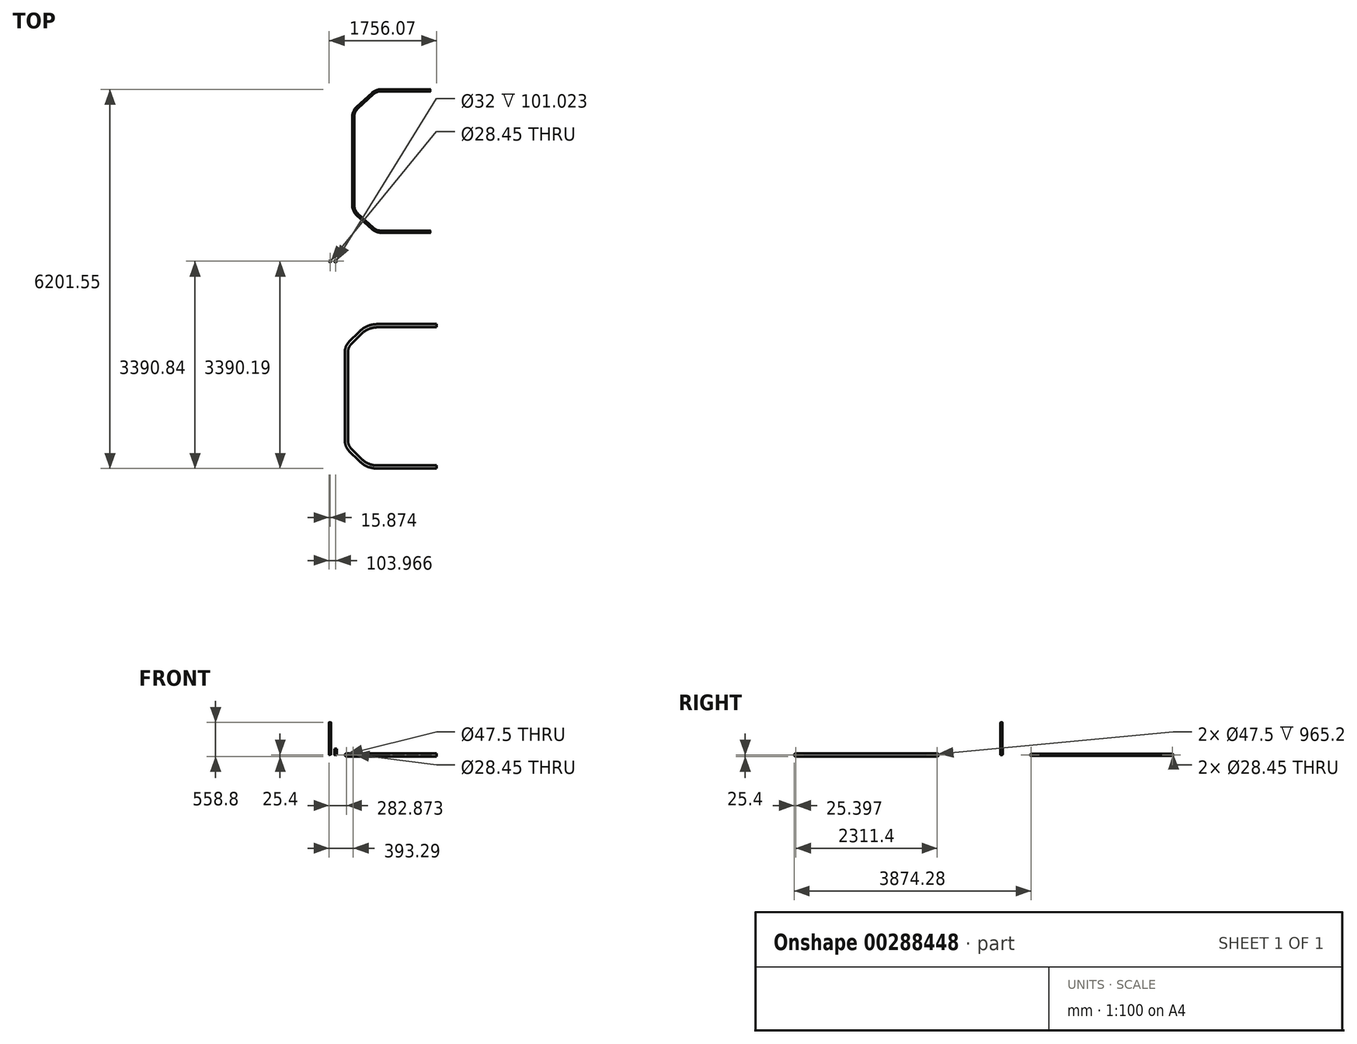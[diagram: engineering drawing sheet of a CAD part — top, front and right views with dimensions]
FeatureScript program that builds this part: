
annotation { "Feature Type Name" : "Feature", "Feature Type Description" : "" }
export const myFeature = defineFeature(function(context is Context, id is Id, definition is map)
    precondition{}
    {
        {
            var Q0;
            Q0=qCreatedBy(makeId("Top.planeOp"),FACE);
            var sketch = newSketch(context, id + "F0", { "sketchPlane" : qUnion([Q0])});
            skLineSegment(sketch, "E0", {"start": v(-110.42, -2096.28) * mm, "end": v(1362.78, -2096.28) * mm, "construction": true});
            skLineSegment(sketch, "E1", {"start": v(1362.78, -2096.28) * mm, "end": v(1362.78, -3251.98) * mm, "construction": true});
            skLineSegment(sketch, "E2", {"start": v(1362.78, -3251.98) * mm, "end": v(397.58, -3251.98) * mm});
            skLineSegment(sketch, "E3", {"start": v(115.74, -3135.24) * mm, "end": v(-50.9, -2968.6) * mm});
            skLineSegment(sketch, "E4", {"start": v(-110.42, -2824.91) * mm, "end": v(-110.42, -2096.28) * mm});
            skPoint(sketch, "E5.visualSharp", {"position": v(-110.42, -2909.08) * mm});
            skArc(sketch, "E5.filletArc", {"start": v(-110.42, -2824.91) * mm, "mid": v(-94.95, -2902.68) * mm, "end": v(-50.9, -2968.6) * mm});
            skPoint(sketch, "E6.visualSharp", {"position": v(232.48, -3251.98) * mm});
            skArc(sketch, "E6.filletArc", {"start": v(115.74, -3135.24) * mm, "mid": v(245.05, -3221.64) * mm, "end": v(397.58, -3251.98) * mm});
            skLineSegment(sketch, "E7.MirrorCS", {"start": v(-110.42, -1367.65) * mm, "end": v(-110.42, -2096.28) * mm});
            skArc(sketch, "E8.MirrorCS", {"start": v(-110.42, -1367.65) * mm, "mid": v(-94.95, -1289.9) * mm, "end": v(-50.9, -1223.97) * mm});
            skLineSegment(sketch, "E9.MirrorCS", {"start": v(115.74, -1057.33) * mm, "end": v(-50.9, -1223.97) * mm});
            skLineSegment(sketch, "E10.MirrorCS", {"start": v(1362.78, -940.58) * mm, "end": v(397.58, -940.58) * mm});
            skArc(sketch, "E11.MirrorCS", {"start": v(115.74, -1057.33) * mm, "mid": v(245.05, -970.92) * mm, "end": v(397.58, -940.58) * mm});
            skPoint(sketch, "E12.MirrorP", {"position": v(232.48, -940.58) * mm});
            skPoint(sketch, "E13.MirrorP", {"position": v(-110.42, -1283.48) * mm});
            skCircle(sketch, "E14", {"center": v(1203.51, -3251.98) * mm, "radius": 16 * mm});
            skCircle(sketch, "E15.0", {"center": v(1203.51, -3251.98) * mm, "radius": 17.65 * mm});
            skSolve(sketch);
        }
        {
            var Q0;
            Q0=qCreatedBy(makeId("Top.planeOp"),FACE);
            var sketch = newSketch(context, id + "F1", { "sketchPlane" : qUnion([Q0])});
            skLineSegment(sketch, "E16", {"start": v(0, 1752.6) * mm, "end": v(1270, 1752.6) * mm, "construction": true});
            skLineSegment(sketch, "E17", {"start": v(1270, 1752.6) * mm, "end": v(1270, 596.9) * mm, "construction": true});
            skLineSegment(sketch, "E18", {"start": v(1270, 596.9) * mm, "end": v(453.74, 596.9) * mm});
            skLineSegment(sketch, "E19", {"start": v(316.58, 650.18) * mm, "end": v(66.04, 879.38) * mm});
            skLineSegment(sketch, "E20", {"start": v(0, 1029.3) * mm, "end": v(0, 1752.6) * mm});
            skPoint(sketch, "E21.visualSharp", {"position": v(0, 939.8) * mm});
            skArc(sketch, "E21.filletArc", {"start": v(0, 1029.3) * mm, "mid": v(17.24, 947.4) * mm, "end": v(66.04, 879.38) * mm});
            skPoint(sketch, "E22.visualSharp", {"position": v(374.81, 596.9) * mm});
            skArc(sketch, "E22.filletArc", {"start": v(316.58, 650.18) * mm, "mid": v(380.17, 610.69) * mm, "end": v(453.74, 596.9) * mm});
            skLineSegment(sketch, "E23.MirrorCS", {"start": v(0, 2475.9) * mm, "end": v(0, 1752.6) * mm});
            skArc(sketch, "E24.MirrorCS", {"start": v(0, 2475.9) * mm, "mid": v(17.24, 2557.8) * mm, "end": v(66.04, 2625.82) * mm});
            skLineSegment(sketch, "E25.MirrorCS", {"start": v(316.58, 2855.02) * mm, "end": v(66.04, 2625.82) * mm});
            skLineSegment(sketch, "E26.MirrorCS", {"start": v(1270, 2908.3) * mm, "end": v(453.74, 2908.3) * mm});
            skArc(sketch, "E27.MirrorCS", {"start": v(316.58, 2855.02) * mm, "mid": v(380.17, 2894.51) * mm, "end": v(453.74, 2908.3) * mm});
            skPoint(sketch, "E28.MirrorP", {"position": v(374.81, 2908.3) * mm});
            skPoint(sketch, "E29.MirrorP", {"position": v(0, 2565.4) * mm});
            skSolve(sketch);
        }
        {
            var Q0;
            Q0=sQuery(id+"F0.wireOp",EDGE,"E1");
            cPlane(context, id + "F2", {"entities" : qUnion([Q0]), "cplaneType" : CPlaneType.LINE_ANGLE, "offset" : 25.4 * mm, "angle" : 90 * degree, "width" : 152.4 * mm, "height" : 152.4 * mm});
        }
        {
            var Q0;
            Q0=qCreatedBy(id+"F2.planeOp",FACE);
            var sketch = newSketch(context, id + "F3", { "sketchPlane" : qUnion([Q0])});
            skPoint(sketch, "E30.0", {"position": v(-3251.98, 0) * mm});
            skCircle(sketch, "E31", {"center": v(-3251.98, 0) * mm, "radius": 25.4 * mm});
            skCircle(sketch, "E32.0", {"center": v(-3251.98, 0) * mm, "radius": 23.75 * mm});
            skSolve(sketch);
        }
        {
            var Q0;
            Q0=makeQuery(id+"F3.imprint","IMPRINT",FACE,{"disambiguationData":[TD([[makeQuery(id+"F3.imprint","IMPRINT",EDGE,{"derivedFrom":sQuery(id+"F3.wireOp",EDGE,"E31")}),1.0]])]});
            var Q1;
            Q1=sQuery(id+"F0.wireOp",EDGE,"E2");
            var Q2;
            Q2=sQuery(id+"F0.wireOp",EDGE,"E6.filletArc");
            var Q3;
            Q3=sQuery(id+"F0.wireOp",EDGE,"E3");
            var Q4;
            Q4=sQuery(id+"F0.wireOp",EDGE,"E5.filletArc");
            var Q5;
            Q5=sQuery(id+"F0.wireOp",EDGE,"E4");
            var Q6;
            Q6=sQuery(id+"F0.wireOp",EDGE,"E7.MirrorCS");
            var Q7;
            Q7=sQuery(id+"F0.wireOp",EDGE,"E8.MirrorCS");
            var Q8;
            Q8=sQuery(id+"F0.wireOp",EDGE,"E9.MirrorCS");
            var Q9;
            Q9=sQuery(id+"F0.wireOp",EDGE,"E11.MirrorCS");
            var Q10;
            Q10=sQuery(id+"F0.wireOp",EDGE,"E10.MirrorCS");
            sweep(context, id + "F4", {"profiles" : qUnion([Q0]), "path" : qUnion([Q1, Q2, Q3, Q4, Q5, Q6, Q7, Q8, Q9, Q10])});
        }
        {
            var Q0;
            Q0=sQuery(id+"F1.wireOp",EDGE,"E17");
            cPlane(context, id + "F5", {"entities" : qUnion([Q0]), "cplaneType" : CPlaneType.LINE_ANGLE, "offset" : 25.4 * mm, "angle" : 90 * degree, "width" : 152.4 * mm, "height" : 152.4 * mm});
        }
        {
            var Q0;
            Q0=qCreatedBy(id+"F5.planeOp",FACE);
            var sketch = newSketch(context, id + "F6", { "sketchPlane" : qUnion([Q0])});
            skPoint(sketch, "E33.0", {"position": v(596.9, 0) * mm});
            skCircle(sketch, "E34", {"center": v(596.9, 0) * mm, "radius": 15.88 * mm});
            skCircle(sketch, "E35.0", {"center": v(596.9, 0) * mm, "radius": 14.22 * mm});
            skSolve(sketch);
        }
        {
            var Q0;
            Q0=makeQuery(id+"F6.imprint","IMPRINT",FACE,{"disambiguationData":[TD([[makeQuery(id+"F6.imprint","IMPRINT",EDGE,{"derivedFrom":sQuery(id+"F6.wireOp",EDGE,"E34")}),1.0]])]});
            var Q1;
            Q1=sQuery(id+"F1.wireOp",EDGE,"E18");
            var Q2;
            Q2=sQuery(id+"F1.wireOp",EDGE,"E22.filletArc");
            var Q3;
            Q3=sQuery(id+"F1.wireOp",EDGE,"E19");
            var Q4;
            Q4=sQuery(id+"F1.wireOp",EDGE,"E21.filletArc");
            var Q5;
            Q5=sQuery(id+"F1.wireOp",EDGE,"E20");
            var Q6;
            Q6=sQuery(id+"F1.wireOp",EDGE,"E23.MirrorCS");
            var Q7;
            Q7=sQuery(id+"F1.wireOp",EDGE,"E24.MirrorCS");
            var Q8;
            Q8=sQuery(id+"F1.wireOp",EDGE,"E25.MirrorCS");
            var Q9;
            Q9=sQuery(id+"F1.wireOp",EDGE,"E27.MirrorCS");
            var Q10;
            Q10=sQuery(id+"F1.wireOp",EDGE,"E26.MirrorCS");
            sweep(context, id + "F7", {"profiles" : qUnion([Q0]), "path" : qUnion([Q1, Q2, Q3, Q4, Q5, Q6, Q7, Q8, Q9, Q10])});
        }
        {
            var Q0;
            Q0=qCreatedBy(makeId("Top.planeOp"),FACE);
            cPlane(context, id + "F8", {"entities" : qUnion([Q0]), "cplaneType" : CPlaneType.OFFSET, "offset" : 152.4 * mm, "width" : 152.4 * mm, "height" : 152.4 * mm});
        }
        {
            var Q0;
            Q0=qCreatedBy(id+"F8.planeOp",FACE);
            var sketch = newSketch(context, id + "F9", { "sketchPlane" : qUnion([Q0])});
            skLineSegment(sketch, "E36.0", {"start": v(1270, 581.02) * mm, "end": v(1270, 612.77) * mm});
            skArc(sketch, "E37", {"start": v(1270, 612.77) * mm, "mid": v(1254.12, 596.9) * mm, "end": v(1270, 581.02) * mm});
            skLineSegment(sketch, "E38.0", {"start": v(1270, 2924.17) * mm, "end": v(1270, 2892.42) * mm});
            skArc(sketch, "E39", {"start": v(1270, 2924.17) * mm, "mid": v(1254.12, 2908.3) * mm, "end": v(1270, 2892.42) * mm});
            skSolve(sketch);
        }
        {
            var Q0;
            Q0=makeQuery(id+"F9.imprint","IMPRINT",FACE,{"disambiguationData":[TD([[makeQuery(id+"F9.imprint","IMPRINT",EDGE,{"derivedFrom":sQuery(id+"F9.wireOp",EDGE,"E38.0")}),-1.0]])]});
            var Q1;
            Q1=makeQuery(id+"F9.imprint","IMPRINT",FACE,{"disambiguationData":[TD([[makeQuery(id+"F9.imprint","IMPRINT",EDGE,{"derivedFrom":sQuery(id+"F9.wireOp",EDGE,"E36.0")}),1.0]])]});
            extrude(context, id + "F10", {"entities" : qUnion([Q0, Q1]), "operationType" : NewBodyOperationType.REMOVE, "oppositeDirection" : true, "depth" : 304.8 * mm});
        }
        {
            var Q0;
            Q0=qCreatedBy(makeId("Top.planeOp"),FACE);
            var sketch = newSketch(context, id + "F11", { "sketchPlane" : qUnion([Q0])});
            skCircle(sketch, "E40", {"center": v(-377.42, 113.46) * mm, "radius": 15.88 * mm});
            skCircle(sketch, "E41.0", {"center": v(-377.42, 113.46) * mm, "radius": 14.22 * mm});
            skCircle(sketch, "E42", {"center": v(-289.32, 112.8) * mm, "radius": 16 * mm});
            skCircle(sketch, "E43.0", {"center": v(-289.32, 112.8) * mm, "radius": 17.65 * mm});
            skSolve(sketch);
        }
        {
            var Q0;
            Q0=makeQuery(id+"F11.imprint","IMPRINT",FACE,{"disambiguationData":[TD([[makeQuery(id+"F11.imprint","IMPRINT",EDGE,{"derivedFrom":sQuery(id+"F11.wireOp",EDGE,"E40")}),1.0]])]});
            extrude(context, id + "F12", {"entities" : qUnion([Q0]), "depth" : 533.4 * mm});
        }
        {
            var Q0;
            Q0=makeQuery(id+"F11.imprint","IMPRINT",FACE,{"disambiguationData":[TD([[makeQuery(id+"F11.imprint","IMPRINT",EDGE,{"derivedFrom":sQuery(id+"F11.wireOp",EDGE,"E42")}),-1.0]])]});
            extrude(context, id + "F13", {"entities" : qUnion([Q0]), "depth" : 101.6 * mm});
        }
        {
            var Q0;
            Q0=qCreatedBy(makeId("Front.planeOp"),FACE);
            var sketch = newSketch(context, id + "F14", { "sketchPlane" : qUnion([Q0])});
            skLineSegment(sketch, "E44.0", {"start": v(-306.98, 0) * mm, "end": v(-271.67, 0) * mm});
            skLineSegment(sketch, "E45.0", {"start": v(-393.3, 0) * mm, "end": v(-361.54, 0) * mm});
            skLineSegment(sketch, "E46.0", {"start": v(-393.3, 533.4) * mm, "end": v(-361.54, 533.4) * mm});
            skArc(sketch, "E47", {"start": v(-271.67, 0) * mm, "mid": v(-289.32, 3.17) * mm, "end": v(-306.98, 0) * mm});
            skArc(sketch, "E48", {"start": v(-361.54, 0) * mm, "mid": v(-377.42, 4.25) * mm, "end": v(-393.3, 0) * mm});
            skArc(sketch, "E49", {"start": v(-393.3, 533.4) * mm, "mid": v(-377.42, 529.15) * mm, "end": v(-361.54, 533.4) * mm});
            skSolve(sketch);
        }
        {
            var Q0;
            Q0=makeQuery(id+"F14.imprint","IMPRINT",FACE,{"disambiguationData":[TD([[makeQuery(id+"F14.imprint","IMPRINT",EDGE,{"derivedFrom":sQuery(id+"F14.wireOp",EDGE,"E46.0")}),-1.0]])]});
            var Q1;
            Q1=makeQuery(id+"F14.imprint","IMPRINT",FACE,{"disambiguationData":[TD([[makeQuery(id+"F14.imprint","IMPRINT",EDGE,{"derivedFrom":sQuery(id+"F14.wireOp",EDGE,"E45.0")}),1.0]])]});
            var Q2;
            Q2=makeQuery(id+"F14.imprint","IMPRINT",FACE,{"disambiguationData":[TD([[makeQuery(id+"F14.imprint","IMPRINT",EDGE,{"derivedFrom":sQuery(id+"F14.wireOp",EDGE,"E44.0")}),1.0]])]});
            extrude(context, id + "F15", {"entities" : qUnion([Q0, Q1, Q2]), "operationType" : NewBodyOperationType.REMOVE, "oppositeDirection" : true, "depth" : 152.4 * mm});
        }
    });
